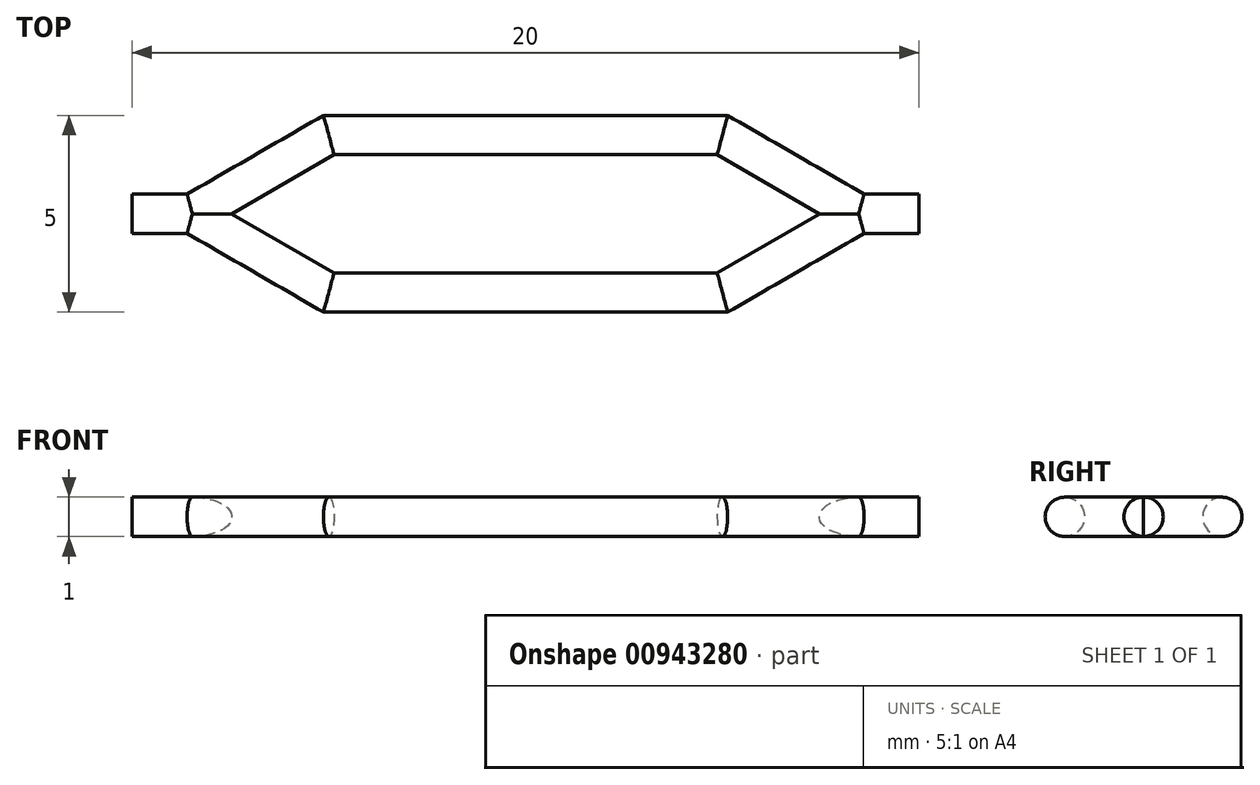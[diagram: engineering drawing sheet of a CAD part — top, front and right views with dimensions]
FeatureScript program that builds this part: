
annotation { "Feature Type Name" : "Feature", "Feature Type Description" : "" }
export const myFeature = defineFeature(function(context is Context, id is Id, definition is map)
    precondition{}
    {
        {
            var Q0;
            Q0=qCreatedBy(makeId("Top.planeOp"),FACE);
            var sketch = newSketch(context, id + "F0", { "sketchPlane" : qUnion([Q0])});
            skLineSegment(sketch, "E0.bottom", {"start": v(0, 20) * mm, "end": v(20, 20) * mm});
            skLineSegment(sketch, "E0.top", {"start": v(0, 0) * mm, "end": v(20, 0) * mm});
            skLineSegment(sketch, "E0.left", {"start": v(0, 20) * mm, "end": v(0, 0) * mm});
            skLineSegment(sketch, "E0.right", {"start": v(20, 20) * mm, "end": v(20, 0) * mm});
            skLineSegment(sketch, "E1", {"start": v(0, 10) * mm, "end": v(20, 10) * mm});
            skLineSegment(sketch, "E2", {"start": v(10, 20) * mm, "end": v(10, 0) * mm});
            skLineSegment(sketch, "E3", {"start": v(0, 10) * mm, "end": v(1.54, 10) * mm});
            skLineSegment(sketch, "E4", {"start": v(1.54, 10) * mm, "end": v(5, 12) * mm});
            skLineSegment(sketch, "E5", {"start": v(5, 12) * mm, "end": v(10, 12) * mm});
            skSolve(sketch);
        }
        {
            var Q0;
            Q0=qCreatedBy(makeId("Right.planeOp"),FACE);
            var sketch = newSketch(context, id + "F1", { "sketchPlane" : qUnion([Q0])});
            skCircle(sketch, "E6", {"center": v(10, 0) * mm, "radius": 0.5 * mm});
            skSolve(sketch);
        }
        {
            var Q0;
            Q0=makeQuery(id+"F1.imprint","IMPRINT",FACE,{"disambiguationData":[TD([[makeQuery(id+"F1.imprint","IMPRINT",EDGE,{"derivedFrom":sQuery(id+"F1.wireOp",EDGE,"E6")}),1.0]])]});
            var Q1;
            Q1=sQuery(id+"F0.wireOp",EDGE,"E3");
            var Q2;
            Q2=sQuery(id+"F0.wireOp",EDGE,"E4");
            var Q3;
            Q3=sQuery(id+"F0.wireOp",EDGE,"E5");
            sweep(context, id + "F2", {"profiles" : qUnion([Q0]), "path" : qUnion([Q1, Q2, Q3])});
        }
        {
            var Q0;
            Q0=sQuery(id+"F0.wireOp",EDGE,"E2");
            cPoint(context, id + "F3", {"entities" : qUnion([Q0]), "parameter" : 0.5});
        }
        {
            var Q0;
            Q0=sQuery(id+"F0.wireOp",EDGE,"E2");
            var Q1;
            Q1 = qCreatedBy(id + "F3" ,VERTEX);
            cPlane(context, id + "F4", {"entities" : qUnion([Q0, Q1]), "cplaneType" : CPlaneType.LINE_POINT, "offset" : 25 * mm, "width" : 150 * mm, "height" : 150 * mm});
        }
        {
            var Q0;
            Q0=sQuery(id+"F0.wireOp",EDGE,"E0.bottom");
            cPoint(context, id + "F5", {"entities" : qUnion([Q0]), "parameter" : 0.5});
        }
        {
            var Q0;
            Q0=sQuery(id+"F0.wireOp",EDGE,"E0.bottom");
            var Q1;
            Q1 = qCreatedBy(id + "F5" ,VERTEX);
            cPlane(context, id + "F6", {"entities" : qUnion([Q0, Q1]), "cplaneType" : CPlaneType.LINE_POINT, "offset" : 25 * mm, "width" : 150 * mm, "height" : 150 * mm});
        }
        {
            var Q0;
            Q0=makeQuery(id+"F2.opSweep","SWEPT_BODY",BODY,{"disambiguationData":[OSD([sQuery(id+"F0.wireOp",EDGE,"E5"),sQuery(id+"F1.wireOp",EDGE,"E6")])]});
            var Q1;
            Q1=qCreatedBy(id+"F6.planeOp",FACE);
            mirror(context, id + "F7", {"operationType" : NewBodyOperationType.ADD, "entities" : qUnion([Q0]), "mirrorPlane" : qUnion([Q1])});
        }
        {
            var Q0;
            Q0=makeQuery(id+"F2.opSweep","SWEPT_BODY",BODY,{"disambiguationData":[OSD([sQuery(id+"F0.wireOp",EDGE,"E5"),sQuery(id+"F1.wireOp",EDGE,"E6")])]});
            var Q1;
            Q1=qCreatedBy(id+"F4.planeOp",FACE);
            mirror(context, id + "F8", {"operationType" : NewBodyOperationType.ADD, "entities" : qUnion([Q0]), "mirrorPlane" : qUnion([Q1])});
        }
    });
